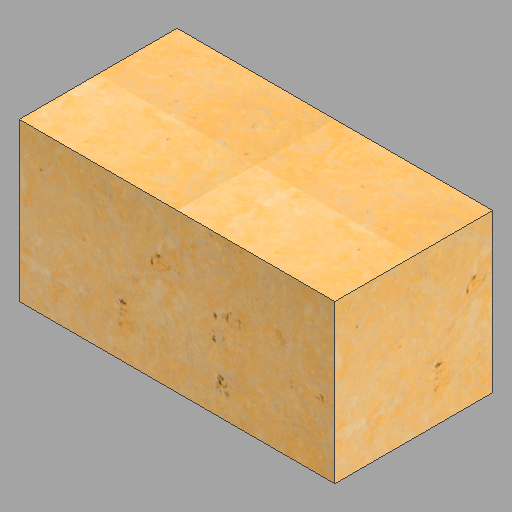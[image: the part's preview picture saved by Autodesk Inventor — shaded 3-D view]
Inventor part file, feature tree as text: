
AUTODESK INVENTOR PART (.ipt)
format: ipt  version: 2023 (Build 270158000, 158)  size: 397,824 bytes
history: native  units: in
note: dims shown in document units (in); Inventor stores cm internally (conversion verified against a paired STEP export)
features: other x1, extrude x1, sketch x1
ambient origin geometry x8: Origin, YZ Plane, XZ Plane, XY Plane, X Axis, Y Axis, Z Axis, Center Point
bodies: Solid1 (feature_tree)
feature tree (3):
  other  "C - 2"
  extrude  "Extrusion1"  Depth=24.0in
  sketch  "Sketch1"  dims[d0=48.0in d1=24.0in d2=24.0in d3=0.0in]
